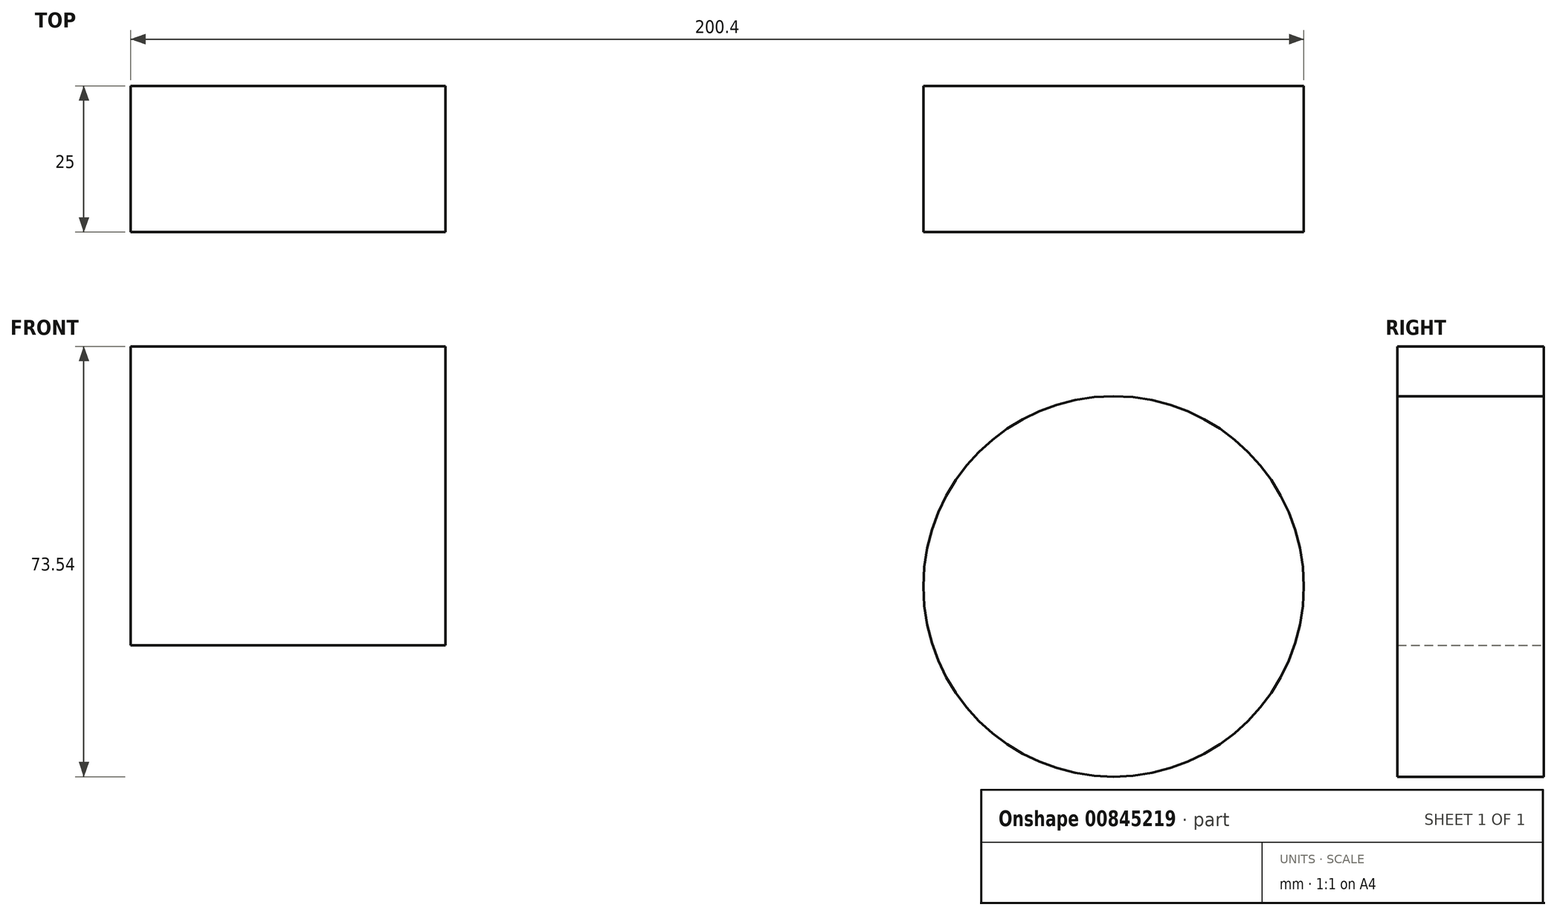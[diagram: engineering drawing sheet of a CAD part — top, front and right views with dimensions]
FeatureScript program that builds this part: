
annotation { "Feature Type Name" : "Feature", "Feature Type Description" : "" }
export const myFeature = defineFeature(function(context is Context, id is Id, definition is map)
    precondition{}
    {
        {
            var Q0;
            Q0=qCreatedBy(makeId("Front.planeOp"),FACE);
            var sketch = newSketch(context, id + "F0", { "sketchPlane" : qUnion([Q0])});
            skLineSegment(sketch, "E0.bottom", {"start": v(-81.4, 41.03) * mm, "end": v(-27.63, 41.03) * mm});
            skLineSegment(sketch, "E0.top", {"start": v(-81.4, -10.07) * mm, "end": v(-27.63, -10.07) * mm});
            skLineSegment(sketch, "E0.left", {"start": v(-81.4, 41.03) * mm, "end": v(-81.4, -10.07) * mm});
            skLineSegment(sketch, "E0.right", {"start": v(-27.63, 41.03) * mm, "end": v(-27.63, -10.07) * mm});
            skSolve(sketch);
        }
        {
            var Q0;
            Q0 = qSketchRegion(id + "F0", true);
            extrude(context, id + "F1", {"entities" : qUnion([Q0]), "depth" : 25 * mm, "offsetDistance" : 25 * mm});
        }
        {
            var Q0;
            Q0=qCreatedBy(makeId("Front.planeOp"),FACE);
            var sketch = newSketch(context, id + "F2", { "sketchPlane" : qUnion([Q0])});
            skCircle(sketch, "E1", {"center": v(86.49, 0) * mm, "radius": 32.5 * mm});
            skSolve(sketch);
        }
        {
            var Q0;
            Q0 = qSketchRegion(id + "F2", true);
            extrude(context, id + "F3", {"entities" : qUnion([Q0]), "depth" : 25 * mm, "offsetDistance" : 25 * mm});
        }
    });
